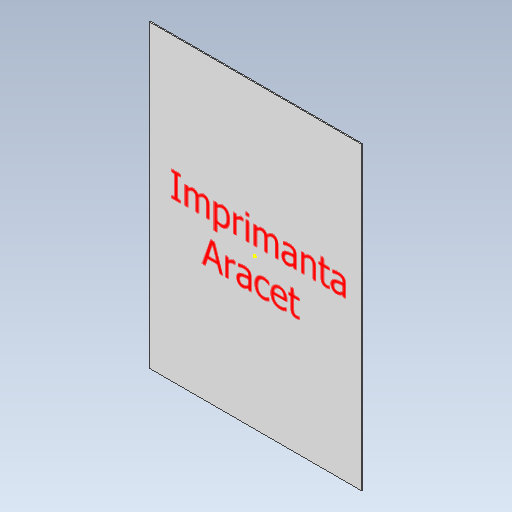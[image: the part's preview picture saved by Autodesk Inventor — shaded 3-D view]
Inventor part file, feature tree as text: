
AUTODESK INVENTOR PART (.ipt)
format: ipt  version: 2020 (Build 240168000, 168)  size: 94,720 bytes
history: native  units: mm
features: sketch x2, extrude x1
ambient origin geometry x8: Origin, YZ Plane, XZ Plane, XY Plane, X Axis, Y Axis, Z Axis, Center Point
bodies: Solid1 (feature_tree)
feature tree (3):
  extrude  "Extrusion1"  Depth=297.0mm
  sketch  "Sketch2"  dims[d2=1.0mm d3=0.0mm]
  sketch  "Sketch1"  dims[d0=210.0mm d1=297.0mm]
